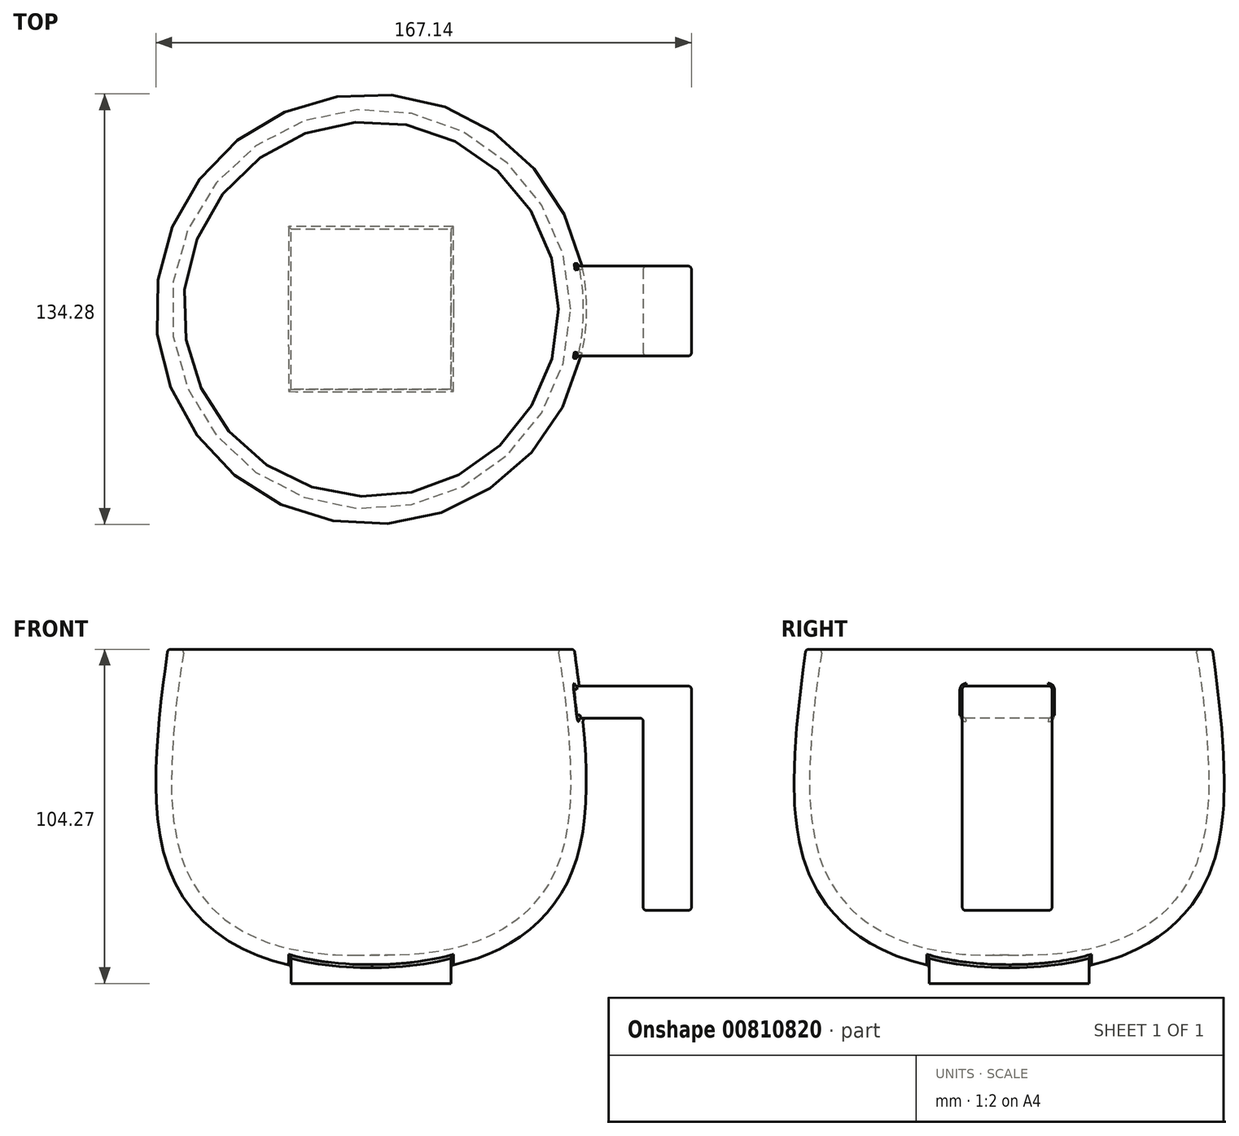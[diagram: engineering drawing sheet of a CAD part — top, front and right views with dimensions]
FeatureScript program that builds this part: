
annotation { "Feature Type Name" : "Feature", "Feature Type Description" : "" }
export const myFeature = defineFeature(function(context is Context, id is Id, definition is map)
    precondition{}
    {
        {
            var Q0;
            Q0=qCreatedBy(makeId("Front.planeOp"),FACE);
            var sketch = newSketch(context, id + "F0", { "sketchPlane" : qUnion([Q0])});
            skFitSpline(sketch, "E0", {"points": [v(62.1, 48.49) * mm, v(62.97, -29.62) * mm, v(31.37, -57.7) * mm, v(-20.84, -59.9) * mm], "startDerivative": vector(32.35, -223.87) * mm, "endDerivative": vector(-171.23, 12.28) * mm});
            skFitSpline(sketch, "E1.0", {"points": [v(57.14, 47.77) * mm, v(58.49, 38.44) * mm, v(60.5, 24.54) * mm, v(62.01, 7.14) * mm, v(62.3, -5.06) * mm, v(61.61, -14.3) * mm, v(60.41, -20.98) * mm, v(59.17, -25.6) * mm, v(57.57, -29.8) * mm, v(55.58, -33.67) * mm, v(53.24, -37.2) * mm, v(49.68, -41.5) * mm, v(45.5, -45.17) * mm, v(40.8, -48.24) * mm, v(37.02, -50.23) * mm, v(33.04, -51.92) * mm, v(28.88, -53.29) * mm, v(24.54, -54.36) * mm, v(18.52, -55.41) * mm, v(10.6, -56.1) * mm, v(0.57, -56.16) * mm, v(-9.82, -55.67) * mm, v(-16.92, -55.17) * mm, v(-20.49, -54.9) * mm]});
            skLineSegment(sketch, "E2", {"start": v(0, 48.93) * mm, "end": v(0, -68.67) * mm});
            skLineSegment(sketch, "E3", {"start": v(41.03, 39.27) * mm, "end": v(97.63, 39.27) * mm});
            skSolve(sketch);
        }
        {
            var Q0;
            {var subQ0=sQuery(id+"F0.wireOp",EDGE,"E2");var subQ1=sQuery(id+"F0.wireOp",EDGE,"E0");var subQ2=makeQuery(id+"F0.imprint","INTERSECT",VERTEX,{"derivedFrom":[subQ1,subQ0]});Q0=makeQuery(id+"F0.imprint","IMPRINT",FACE,{"disambiguationData":[TD([[makeQuery(id+"F0.imprint","IMPRINT",EDGE,{"disambiguationData":[TD([[subQ2,1.0]])],"derivedFrom":subQ1}),-1.0]])]});}
            var Q1;
            Q1=sQuery(id+"F0.wireOp",EDGE,"E2");
            revolve(context, id + "F1", {"surfaceOperationType" : NewSurfaceOperationType.NEW, "entities" : qUnion([Q0]), "axis" : qUnion([Q1]), "revolveType" : RevolveType.FULL});
        }
        {
            var Q0;
            Q0=qCreatedBy(makeId("Front.planeOp"),FACE);
            cPlane(context, id + "F2", {"entities" : qUnion([Q0]), "cplaneType" : CPlaneType.OFFSET, "offset" : 70 * mm, "width" : 150 * mm, "height" : 150 * mm});
        }
        {
            var Q0;
            Q0=qCreatedBy(id+"F2.planeOp",FACE);
            var sketch = newSketch(context, id + "F3", { "sketchPlane" : qUnion([Q0])});
            skText(sketch, "E4", { "text": "PJH\n", "fontName": "OpenSans-Regular.ttf"});
            const initialGuessF3  = {"E4": [-0.03645, -0.03335, 1, 0, 0.03335]};
            skSetInitialGuess(sketch, initialGuessF3);
            skSolve(sketch);
        }
        {
            var Q0;
            Q0 = qSketchRegion(id + "F3", true);
            var Q1;
            Q1 = qConstructionFilter(qBodyType(qCreatedBy(id + "F3" ,EDGE), BodyType.WIRE), ConstructionObject.NO);
            extrude(context, id + "F4", {"entities" : qUnion([Q0]), "bodyType" : ToolBodyType.SURFACE, "surfaceEntities" : qUnion([Q1]), "endBound" : BoundingType.UP_TO_NEXT, "oppositeDirection" : true, "depth" : 25 * mm, "offsetDistance" : 25 * mm});
        }
        {
            var Q0;
            Q0=qCreatedBy(makeId("Right.planeOp"),FACE);
            cPlane(context, id + "F5", {"entities" : qUnion([Q0]), "cplaneType" : CPlaneType.OFFSET, "offset" : 100 * mm, "width" : 150 * mm, "height" : 150 * mm});
        }
        {
            var Q0;
            Q0=qCreatedBy(id+"F5.planeOp",FACE);
            var sketch = newSketch(context, id + "F6", { "sketchPlane" : qUnion([Q0])});
            skLineSegment(sketch, "E5.bottom", {"start": v(-14.62, 27.77) * mm, "end": v(13.38, 27.77) * mm});
            skLineSegment(sketch, "E5.top", {"start": v(-14.62, 17.77) * mm, "end": v(13.38, 17.77) * mm});
            skLineSegment(sketch, "E5.left", {"start": v(-14.62, 27.77) * mm, "end": v(-14.62, 17.77) * mm});
            skLineSegment(sketch, "E5.right", {"start": v(13.38, 27.77) * mm, "end": v(13.38, 17.77) * mm});
            skSolve(sketch);
        }
        {
            var Q0;
            Q0=makeQuery(id+"F6.imprint","IMPRINT",FACE,{"disambiguationData":[TD([[makeQuery(id+"F6.imprint","IMPRINT",EDGE,{"derivedFrom":sQuery(id+"F6.wireOp",EDGE,"E5.bottom")}),-1.0]])]});
            extrude(context, id + "F7", {"entities" : qUnion([Q0]), "operationType" : NewBodyOperationType.ADD, "endBound" : BoundingType.UP_TO_NEXT, "oppositeDirection" : true, "depth" : 25 * mm, "offsetDistance" : 25 * mm});
        }
        {
            var Q0;
            Q0=makeQuery(id+"F7.opExtrude","SWEPT_FACE",FACE,{"disambiguationData":[OSD([sQuery(id+"F6.wireOp",EDGE,"E5.bottom")])]});
            var sketch = newSketch(context, id + "F8", { "sketchPlane" : qUnion([Q0])});
            skLineSegment(sketch, "E6.bottom", {"start": v(84.93, -14.62) * mm, "end": v(100, -14.62) * mm});
            skLineSegment(sketch, "E6.top", {"start": v(84.93, 13.38) * mm, "end": v(100, 13.38) * mm});
            skLineSegment(sketch, "E6.left", {"start": v(84.93, -14.62) * mm, "end": v(84.93, 13.38) * mm});
            skLineSegment(sketch, "E6.right", {"start": v(100, -14.62) * mm, "end": v(100, 13.38) * mm});
            skSolve(sketch);
        }
        {
            var Q0;
            Q0=makeQuery(id+"F8.imprint","IMPRINT",FACE,{"disambiguationData":[TD([[makeQuery(id+"F8.imprint","IMPRINT",EDGE,{"derivedFrom":sQuery(id+"F8.wireOp",EDGE,"E6.bottom")}),1.0]])]});
            extrude(context, id + "F9", {"entities" : qUnion([Q0]), "operationType" : NewBodyOperationType.ADD, "oppositeDirection" : true, "depth" : 70 * mm, "offsetDistance" : 25 * mm});
        }
        {
            var Q0;
            Q0=qCreatedBy(makeId("Top.planeOp"),FACE);
            cPlane(context, id + "F10", {"entities" : qUnion([Q0]), "cplaneType" : CPlaneType.OFFSET, "offset" : 65 * mm, "oppositeDirection" : true, "width" : 150 * mm, "height" : 150 * mm});
        }
        {
            var Q0;
            Q0=qCreatedBy(id+"F10.planeOp",FACE);
            var sketch = newSketch(context, id + "F11", { "sketchPlane" : qUnion([Q0])});
            skLineSegment(sketch, "E7.bottom", {"start": v(-25, -25) * mm, "end": v(25, -25) * mm});
            skLineSegment(sketch, "E7.top", {"start": v(-25, 25) * mm, "end": v(25, 25) * mm});
            skLineSegment(sketch, "E7.left", {"start": v(-25, -25) * mm, "end": v(-25, 25) * mm});
            skLineSegment(sketch, "E7.right", {"start": v(25, -25) * mm, "end": v(25, 25) * mm});
            skSolve(sketch);
        }
        {
            var Q0;
            Q0=makeQuery(id+"F11.imprint","IMPRINT",FACE,{"disambiguationData":[TD([[makeQuery(id+"F11.imprint","IMPRINT",EDGE,{"derivedFrom":sQuery(id+"F11.wireOp",EDGE,"E7.bottom")}),1.0]])]});
            extrude(context, id + "F12", {"entities" : qUnion([Q0]), "operationType" : NewBodyOperationType.ADD, "endBound" : BoundingType.UP_TO_NEXT, "depth" : 25 * mm, "offsetDistance" : 25 * mm});
        }
        {
            var Q0;
            Q0=makeQuery(id+"F1.opRevolve","SWEPT_FACE",FACE,{"disambiguationData":[OSD([sQuery(id+"F0.wireOp",EDGE,"E0")])]});
            var Q1;
            Q1=makeQuery(id+"F9.boolean.opBoolean","MERGE",FACE,{"derivedFrom":[makeQuery(id+"F7.opExtrude","SWEPT_FACE",FACE,{"disambiguationData":[OSD([sQuery(id+"F6.wireOp",EDGE,"E5.left")])]}),makeQuery(id+"F9.opExtrude","SWEPT_FACE",FACE,{"disambiguationData":[OSD([sQuery(id+"F8.wireOp",EDGE,"E6.bottom")])]})]});
            var Q2;
            Q2=makeQuery(id+"F9.boolean.opBoolean","MERGE",FACE,{"derivedFrom":[makeQuery(id+"F7.opExtrude","CAP_FACE",FACE,{"disambiguationData":[OSD([sQuery(id+"F6.wireOp",EDGE,"E5.bottom"),sQuery(id+"F6.wireOp",EDGE,"E5.top"),sQuery(id+"F6.wireOp",EDGE,"E5.left"),sQuery(id+"F6.wireOp",EDGE,"E5.right")])],"isStart":true}),makeQuery(id+"F9.opExtrude","SWEPT_FACE",FACE,{"disambiguationData":[OSD([sQuery(id+"F8.wireOp",EDGE,"E6.right")])]})]});
            var Q3;
            Q3=makeQuery(id+"F9.boolean.opBoolean","MERGE",FACE,{"derivedFrom":[makeQuery(id+"F7.opExtrude","SWEPT_FACE",FACE,{"disambiguationData":[OSD([sQuery(id+"F6.wireOp",EDGE,"E5.right")])]}),makeQuery(id+"F9.opExtrude","SWEPT_FACE",FACE,{"disambiguationData":[OSD([sQuery(id+"F8.wireOp",EDGE,"E6.top")])]})]});
            var Q4;
            Q4=makeQuery(id+"F9.opExtrude","CAP_FACE",FACE,{"disambiguationData":[OSD([sQuery(id+"F8.wireOp",EDGE,"E6.bottom"),sQuery(id+"F8.wireOp",EDGE,"E6.top"),sQuery(id+"F8.wireOp",EDGE,"E6.left"),sQuery(id+"F8.wireOp",EDGE,"E6.right")])],"isStart":false});
            var Q5;
            Q5=makeQuery(id+"F9.opExtrude","SWEPT_FACE",FACE,{"disambiguationData":[OSD([sQuery(id+"F8.wireOp",EDGE,"E6.left")])]});
            var Q6;
            Q6=makeQuery(id+"F7.opExtrude","SWEPT_FACE",FACE,{"disambiguationData":[OSD([sQuery(id+"F6.wireOp",EDGE,"E5.top")])]});
            var Q7;
            Q7=makeQuery(id+"F1.opRevolve","SWEPT_EDGE",EDGE,{"disambiguationData":[OSD([sQuery(id+"F0.wireOp",EDGE,"E1.0"),sQuery(id+"F0.wireOp",EDGE,"E3")])]});
            var Q8;
            Q8=makeQuery(id+"F1.opRevolve","SWEPT_EDGE",EDGE,{"disambiguationData":[OSD([sQuery(id+"F0.wireOp",EDGE,"E0"),sQuery(id+"F0.wireOp",EDGE,"E3")])]});
            fillet(context, id + "F13", {"entities" : qUnion([Q0, Q1, Q2, Q3, Q4, Q5, Q6, Q7, Q8]), "radius" : 1 * mm, "tangentPropagation" : true, "allowEdgeOverflow" : false});
        }
    });
